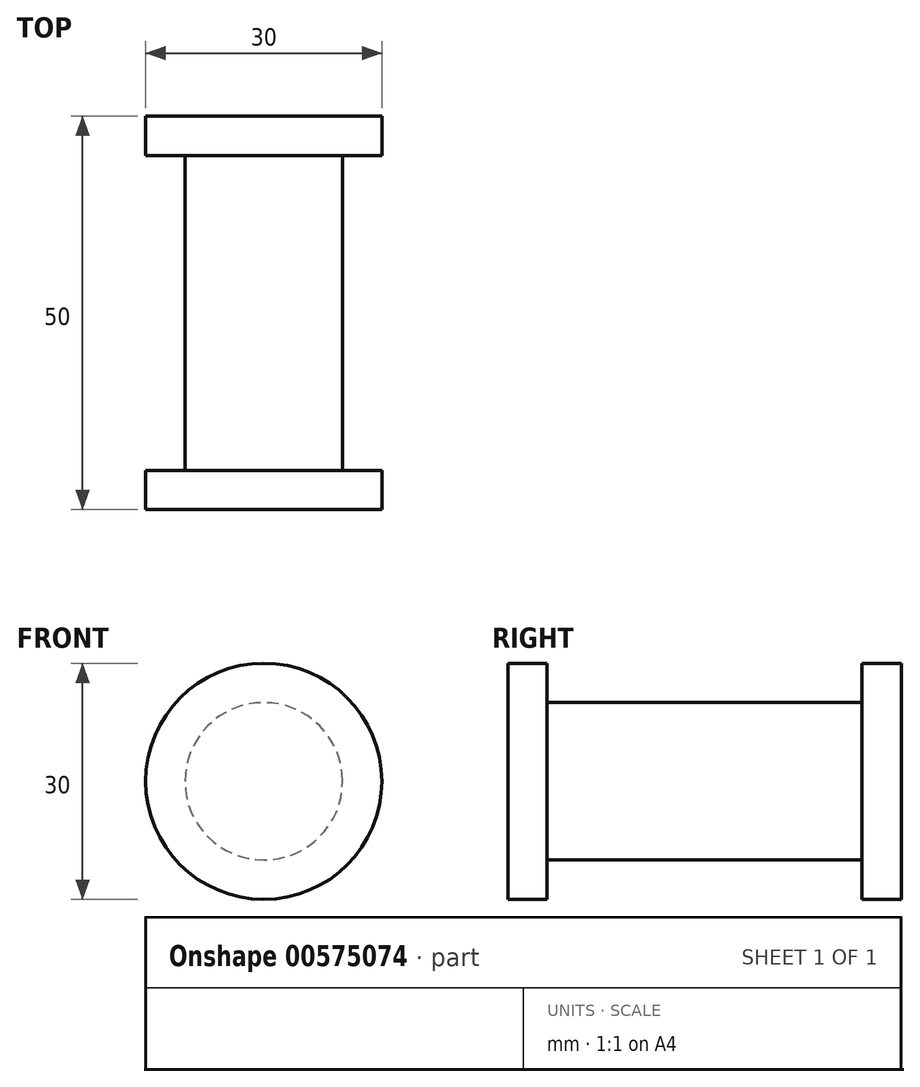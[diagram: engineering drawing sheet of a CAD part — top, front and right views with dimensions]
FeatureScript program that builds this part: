
annotation { "Feature Type Name" : "Feature", "Feature Type Description" : "" }
export const myFeature = defineFeature(function(context is Context, id is Id, definition is map)
    precondition{}
    {
        {
            var Q0;
            Q0=qCreatedBy(makeId("Front.planeOp"),FACE);
            var sketch = newSketch(context, id + "F0", { "sketchPlane" : qUnion([Q0])});
            skCircle(sketch, "E0", {"center": v(0, 0) * mm, "radius": 10 * mm});
            skSolve(sketch);
        }
        {
            var Q0;
            Q0 = qSketchRegion(id + "F0", true);
            extrude(context, id + "F1", {"entities" : qUnion([Q0]), "depth" : 20 * mm, "offsetDistance" : 25 * mm});
        }
        {
            var Q0;
            Q0=makeQuery(id+"F1.opExtrude","CAP_FACE",FACE,{"disambiguationData":[OSD([sQuery(id+"F0.wireOp",EDGE,"E0")])],"isStart":false});
            var sketch = newSketch(context, id + "F2", { "sketchPlane" : qUnion([Q0])});
            skCircle(sketch, "E1", {"center": v(0, 0) * mm, "radius": 15 * mm});
            skSolve(sketch);
        }
        {
            var Q0;
            Q0 = qSketchRegion(id + "F2", true);
            extrude(context, id + "F3", {"entities" : qUnion([Q0]), "operationType" : NewBodyOperationType.ADD, "depth" : 5 * mm, "offsetDistance" : 25 * mm});
        }
        {
            var Q0;
            Q0=makeQuery(id+"F1.opExtrude","SWEPT_BODY",BODY,{"disambiguationData":[OSD([sQuery(id+"F0.wireOp",EDGE,"E0")])]});
            var Q1;
            Q1=makeQuery(id+"F1.opExtrude","CAP_FACE",FACE,{"disambiguationData":[OSD([sQuery(id+"F0.wireOp",EDGE,"E0")])],"isStart":true});
            mirror(context, id + "F4", {"operationType" : NewBodyOperationType.ADD, "entities" : qUnion([Q0]), "mirrorPlane" : qUnion([Q1])});
        }
    });
